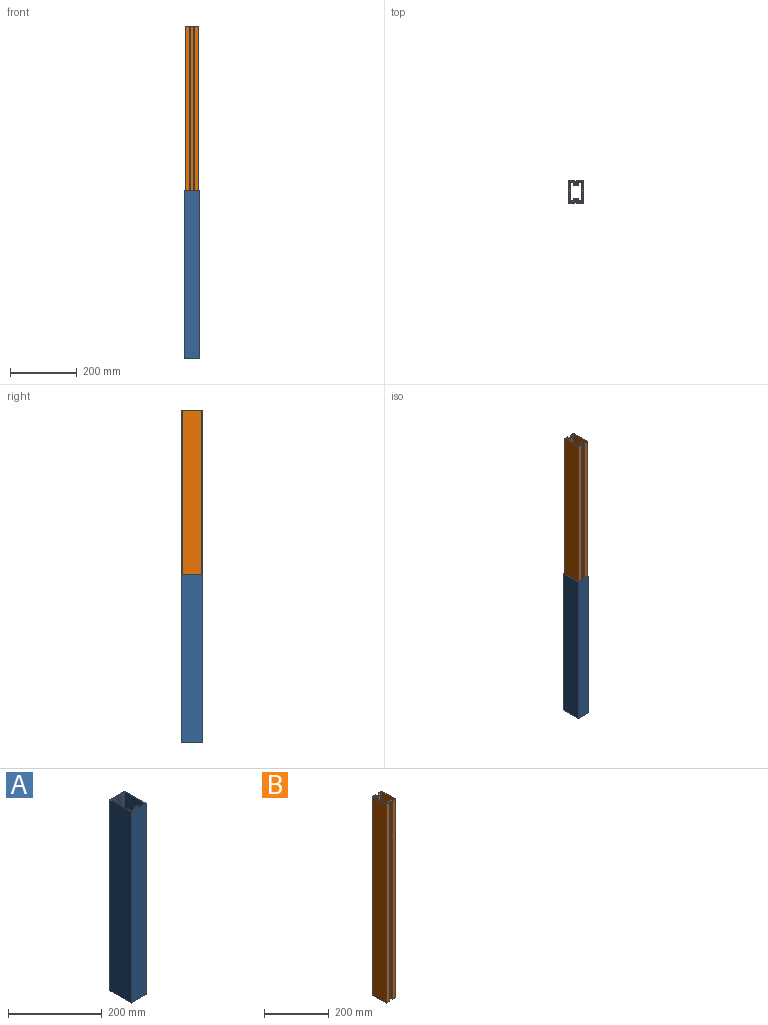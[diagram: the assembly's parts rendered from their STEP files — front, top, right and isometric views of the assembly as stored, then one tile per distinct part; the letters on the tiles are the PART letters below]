
ASSEMBLY  parts=2 mates=1
PART A: 46 faces, bbox 45x65x500 mm
  f0: plane 500x43.8mm, normal (0,1,0), area 21900mm2, adj f1,f43,f44,f45
  f1: cylinder r=0.6mm len=500mm, axis (0,0,-1), area 471.2mm2, adj f0,f2,f44,f45
  f2: plane 500x63.8mm, normal (-1,0,0), area 31900mm2, adj f1,f3,f44,f45
  f3: cylinder r=0.6mm len=500mm, axis (0,0,-1), area 471.2mm2, adj f2,f4,f44,f45
  f4: plane 500x43.8mm, normal (0,-1,0), area 21900mm2, adj f3,f5,f44,f45
  f5: cylinder r=0.6mm len=500mm, axis (0,0,-1), area 471.2mm2, adj f4,f6,f44,f45
  f6: plane 500x63.8mm, normal (1,0,0), area 31900mm2, adj f5,f43,f44,f45
  f7: cylinder r=0.5mm len=500mm, axis (0,0,-1), area 392.7mm2, adj f8,f42,f44,f45
  f8: plane 500x14.5mm, normal (0,-1,0), area 7250mm2, adj f7,f9,f44,f45
  f9: cylinder r=0.5mm len=500mm, axis (0,0,-1), area 392.7mm2, adj f8,f10,f44,f45
  f10: plane 500x60mm, normal (-1,0,0), area 30000mm2, adj f9,f11,f44,f45
  f11: cylinder r=0.5mm len=500mm, axis (0,0,-1), area 392.7mm2, adj f10,f12,f44,f45
  f12: plane 500x14.5mm, normal (0,1,0), area 7250mm2, adj f11,f13,f44,f45
  f13: cylinder r=0.5mm len=500mm, axis (0,0,-1), area 392.7mm2, adj f12,f14,f44,f45
  f14: plane 500x2mm, normal (1,0,0), area 1000mm2, adj f13,f15,f44,f45
  f15: cylinder r=5mm len=500mm, axis (0,0,-1), area 2775.6mm2, adj f14,f16,f44,f45
  f16: cylinder r=0.5mm len=500mm, axis (0,0,-1), area 507.8mm2, adj f15,f17,f44,f45
  f17: plane 500x1.66mm, normal (-1,0,0), area 831.3mm2, adj f16,f18,f44,f45
  f18: cylinder r=0.5mm len=500mm, axis (0,0,-1), area 217.4mm2, adj f17,f19,f44,f45
  f19: cylinder r=2.6mm len=500mm, axis (0,0,-1), area 6344.9mm2, adj f18,f20,f44,f45
  f20: cylinder r=0.5mm len=500mm, axis (0,0,-1), area 217.4mm2, adj f19,f21,f44,f45
  f21: plane 500x1.66mm, normal (1,0,0), area 831.3mm2, adj f20,f22,f44,f45
  f22: cylinder r=0.5mm len=500mm, axis (0,0,-1), area 507.8mm2, adj f21,f23,f44,f45
  f23: cylinder r=5mm len=500mm, axis (0,0,-1), area 2775.6mm2, adj f22,f24,f44,f45
  f24: plane 500x2mm, normal (-1,0,0), area 1000mm2, adj f23,f25,f44,f45
  f25: cylinder r=0.5mm len=500mm, axis (0,0,-1), area 392.7mm2, adj f24,f26,f44,f45
  f26: plane 500x14.5mm, normal (0,1,0), area 7250mm2, adj f25,f27,f44,f45
  f27: cylinder r=0.5mm len=500mm, axis (0,0,-1), area 392.7mm2, adj f26,f28,f44,f45
  f28: plane 500x60mm, normal (1,0,0), area 30000mm2, adj f27,f29,f44,f45
  f29: cylinder r=0.5mm len=500mm, axis (0,0,-1), area 392.7mm2, adj f28,f30,f44,f45
  f30: plane 500x14.5mm, normal (0,-1,0), area 7250mm2, adj f29,f31,f44,f45
  f31: cylinder r=0.5mm len=500mm, axis (0,0,-1), area 392.7mm2, adj f30,f32,f44,f45
  f32: plane 500x2mm, normal (-1,0,0), area 1000mm2, adj f31,f33,f44,f45
  f33: cylinder r=5mm len=500mm, axis (0,0,-1), area 2775.6mm2, adj f32,f34,f44,f45
  f34: cylinder r=0.5mm len=500mm, axis (0,0,-1), area 507.8mm2, adj f33,f35,f44,f45
  f35: plane 500x1.66mm, normal (1,0,0), area 831.3mm2, adj f34,f36,f44,f45
  f36: cylinder r=0.5mm len=500mm, axis (0,0,-1), area 217.4mm2, adj f35,f37,f44,f45
  f37: cylinder r=2.6mm len=500mm, axis (0,0,-1), area 6344.9mm2, adj f36,f38,f44,f45
  f38: cylinder r=0.5mm len=500mm, axis (0,0,-1), area 217.4mm2, adj f37,f39,f44,f45
  f39: plane 500x1.66mm, normal (-1,0,0), area 831.3mm2, adj f38,f40,f44,f45
  f40: cylinder r=0.5mm len=500mm, axis (0,0,-1), area 507.8mm2, adj f39,f41,f44,f45
  f41: cylinder r=5mm len=500mm, axis (0,0,-1), area 2775.6mm2, adj f40,f42,f44,f45
  f42: plane 500x2mm, normal (1,0,0), area 1000mm2, adj f7,f41,f44,f45
  f43: cylinder r=0.6mm len=500mm, axis (0,0,-1), area 471.2mm2, adj f0,f6,f44,f45
  f44: plane 65x45mm, normal (0,0,1), area 494.8mm2, adj f0,f1,f2,f3,f4,f5,f6,f7
  f45: plane 65x45mm, normal (0,0,-1), area 494.8mm2, adj f0,f1,f2,f3,f4,f5,f6,f7
PART B: 42 faces, bbox 40.6x60.6x750 mm
  f0: plane 750x13.8mm, normal (0,1,0), area 10350mm2, adj f1,f39,f40,f41
  f1: cylinder r=0.5mm len=750mm, axis (0,0,-1), area 589mm2, adj f0,f2,f40,f41
  f2: plane 750x59.6mm, normal (-1,0,0), area 44700mm2, adj f1,f3,f40,f41
  f3: cylinder r=0.5mm len=750mm, axis (0,0,-1), area 589mm2, adj f2,f4,f40,f41
  f4: plane 750x13.8mm, normal (0,-1,0), area 10350mm2, adj f3,f5,f40,f41
  f5: cylinder r=0.5mm len=750mm, axis (0,0,-1), area 589mm2, adj f4,f6,f40,f41
  f6: plane 750x7mm, normal (1,0,0), area 5250mm2, adj f5,f7,f40,f41
  f7: cylinder r=0.5mm len=750mm, axis (0,0,-1), area 589mm2, adj f6,f8,f40,f41
  f8: plane 750x10mm, normal (0,-1,0), area 7500mm2, adj f7,f9,f40,f41
  f9: cylinder r=0.5mm len=750mm, axis (0,0,-1), area 589mm2, adj f8,f10,f40,f41
  f10: plane 750x7mm, normal (-1,0,0), area 5250mm2, adj f9,f11,f40,f41
  f11: cylinder r=0.5mm len=750mm, axis (0,0,-1), area 589mm2, adj f10,f12,f40,f41
  f12: plane 750x13.8mm, normal (0,-1,0), area 10350mm2, adj f11,f13,f40,f41
  f13: cylinder r=0.5mm len=750mm, axis (0,0,-1), area 589mm2, adj f12,f14,f40,f41
  f14: plane 750x59.6mm, normal (1,0,0), area 44700mm2, adj f13,f15,f40,f41
  f15: cylinder r=0.5mm len=750mm, axis (0,0,-1), area 589mm2, adj f14,f16,f40,f41
  f16: plane 750x13.8mm, normal (0,1,0), area 10350mm2, adj f15,f17,f40,f41
  f17: cylinder r=0.5mm len=750mm, axis (0,0,-1), area 589mm2, adj f16,f18,f40,f41
  f18: plane 750x7mm, normal (-1,0,0), area 5250mm2, adj f17,f19,f40,f41
  f19: cylinder r=0.5mm len=750mm, axis (0,0,-1), area 589mm2, adj f18,f20,f40,f41
  f20: plane 750x10mm, normal (0,1,0), area 7500mm2, adj f19,f21,f40,f41
  f21: cylinder r=0.5mm len=750mm, axis (0,0,-1), area 589mm2, adj f20,f22,f40,f41
  f22: plane 750x7mm, normal (1,0,0), area 5250mm2, adj f21,f39,f40,f41
  f23: plane 750x55.6mm, normal (-1,0,0), area 41700mm2, adj f24,f38,f40,f41
  f24: plane 750x9.8mm, normal (0,1,0), area 7350mm2, adj f23,f25,f40,f41
  f25: plane 750x5mm, normal (1,0,0), area 3750mm2, adj f24,f26,f40,f41
  f26: cylinder r=3mm len=750mm, axis (0,0,-1), area 3534.3mm2, adj f25,f27,f40,f41
  f27: plane 750x10mm, normal (0,1,0), area 7500mm2, adj f26,f28,f40,f41
  f28: cylinder r=3mm len=750mm, axis (0,0,-1), area 3534.3mm2, adj f27,f29,f40,f41
  f29: plane 750x5mm, normal (-1,0,0), area 3750mm2, adj f28,f30,f40,f41
  f30: plane 750x9.8mm, normal (0,1,0), area 7350mm2, adj f29,f31,f40,f41
  f31: plane 750x55.6mm, normal (1,0,0), area 41700mm2, adj f30,f32,f40,f41
  f32: plane 750x9.8mm, normal (0,-1,0), area 7350mm2, adj f31,f33,f40,f41
  f33: plane 750x5mm, normal (-1,0,0), area 3750mm2, adj f32,f34,f40,f41
  f34: cylinder r=3mm len=750mm, axis (0,0,-1), area 3534.3mm2, adj f33,f35,f40,f41
  f35: plane 750x10mm, normal (0,-1,0), area 7500mm2, adj f34,f36,f40,f41
  f36: cylinder r=3mm len=750mm, axis (0,0,-1), area 3534.3mm2, adj f35,f37,f40,f41
  f37: plane 750x5mm, normal (1,0,0), area 3750mm2, adj f36,f38,f40,f41
  f38: plane 750x9.8mm, normal (0,-1,0), area 7350mm2, adj f23,f37,f40,f41
  f39: cylinder r=0.5mm len=750mm, axis (0,0,-1), area 589mm2, adj f0,f22,f40,f41
  f40: plane 60.6x40.6mm, normal (0,0,1), area 553.1mm2, adj f0,f1,f2,f3,f4,f5,f6,f7
  f41: plane 60.6x40.6mm, normal (0,0,-1), area 553.1mm2, adj f0,f1,f2,f3,f4,f5,f6,f7
PLACE A t=(-301.16,709.95,329.37)mm
PLACE B t=(-278.66,742.45,573.09)mm
MATE slider A.f45 <-> B.f41  axis (0,0,-1) through (-278.66,742.45,329.37)mm
